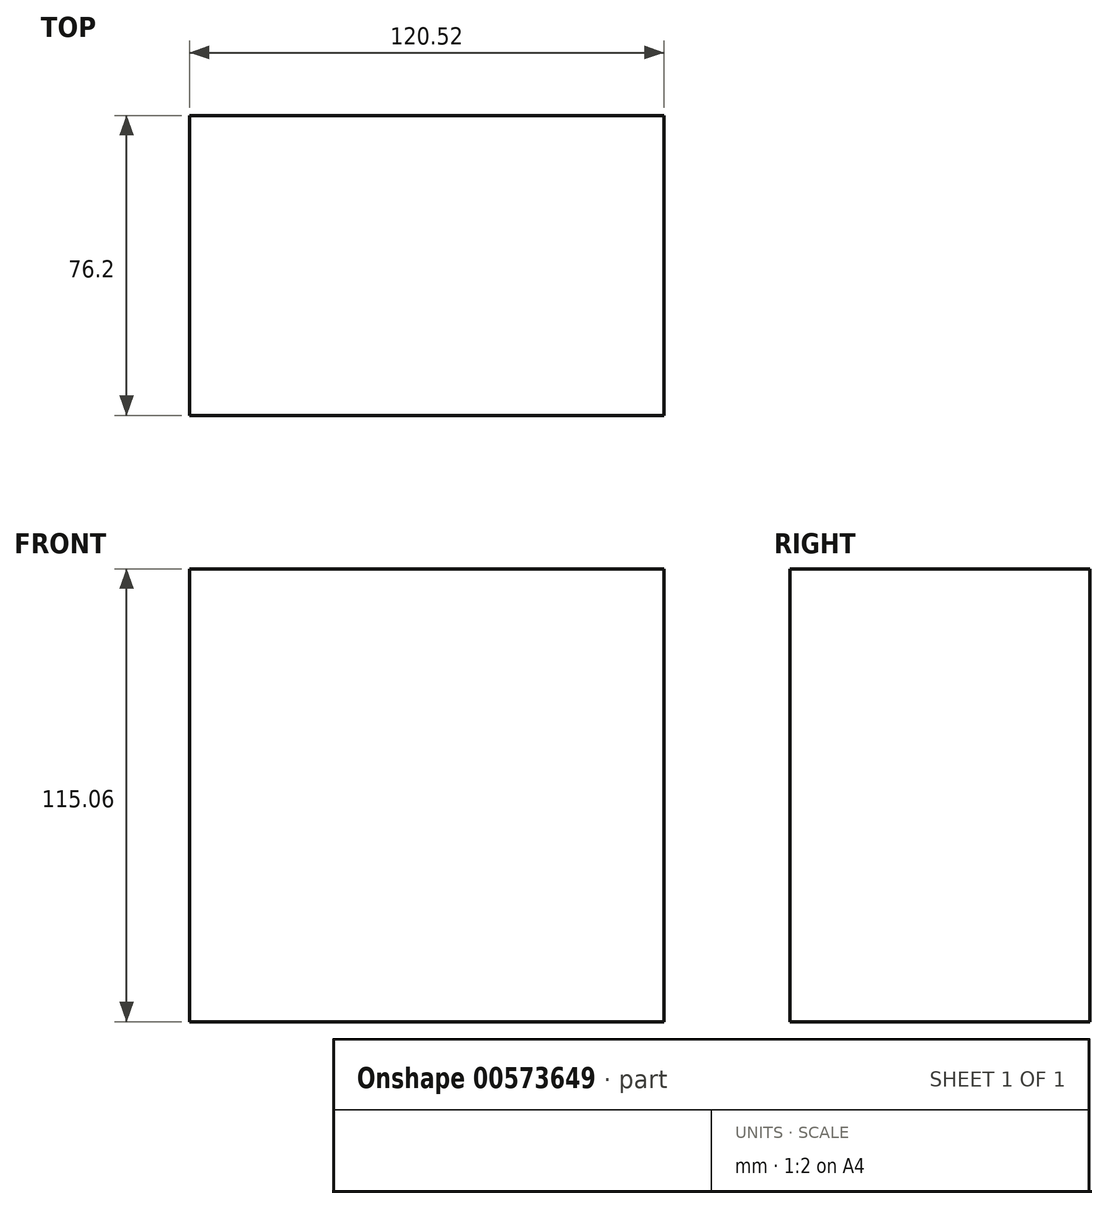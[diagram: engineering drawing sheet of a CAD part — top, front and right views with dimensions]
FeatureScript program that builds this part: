
annotation { "Feature Type Name" : "Feature", "Feature Type Description" : "" }
export const myFeature = defineFeature(function(context is Context, id is Id, definition is map)
    precondition{}
    {
        {
            var Q0;
            Q0=qCreatedBy(makeId("Front.planeOp"),FACE);
            var sketch = newSketch(context, id + "F0", { "sketchPlane" : qUnion([Q0])});
            skLineSegment(sketch, "E0.bottom", {"start": v(60.26, 57.53) * mm, "end": v(-60.26, 57.53) * mm});
            skLineSegment(sketch, "E0.top", {"start": v(60.26, -57.53) * mm, "end": v(-60.26, -57.53) * mm});
            skLineSegment(sketch, "E0.left", {"start": v(60.26, 57.53) * mm, "end": v(60.26, -57.53) * mm});
            skLineSegment(sketch, "E0.right", {"start": v(-60.26, 57.53) * mm, "end": v(-60.26, -57.53) * mm});
            skPoint(sketch, "E0.middle", {"position": v(0, 0) * mm});
            skSolve(sketch);
        }
        {
            var Q0;
            Q0=makeQuery(id+"F0.imprint","IMPRINT",FACE,{"disambiguationData":[TD([[makeQuery(id+"F0.imprint","IMPRINT",EDGE,{"derivedFrom":sQuery(id+"F0.wireOp",EDGE,"E0.bottom")}),1.0]])]});
            extrude(context, id + "F1", {"entities" : qUnion([Q0]), "depth" : 76.2 * mm, "offsetDistance" : 25.4 * mm});
        }
    });
